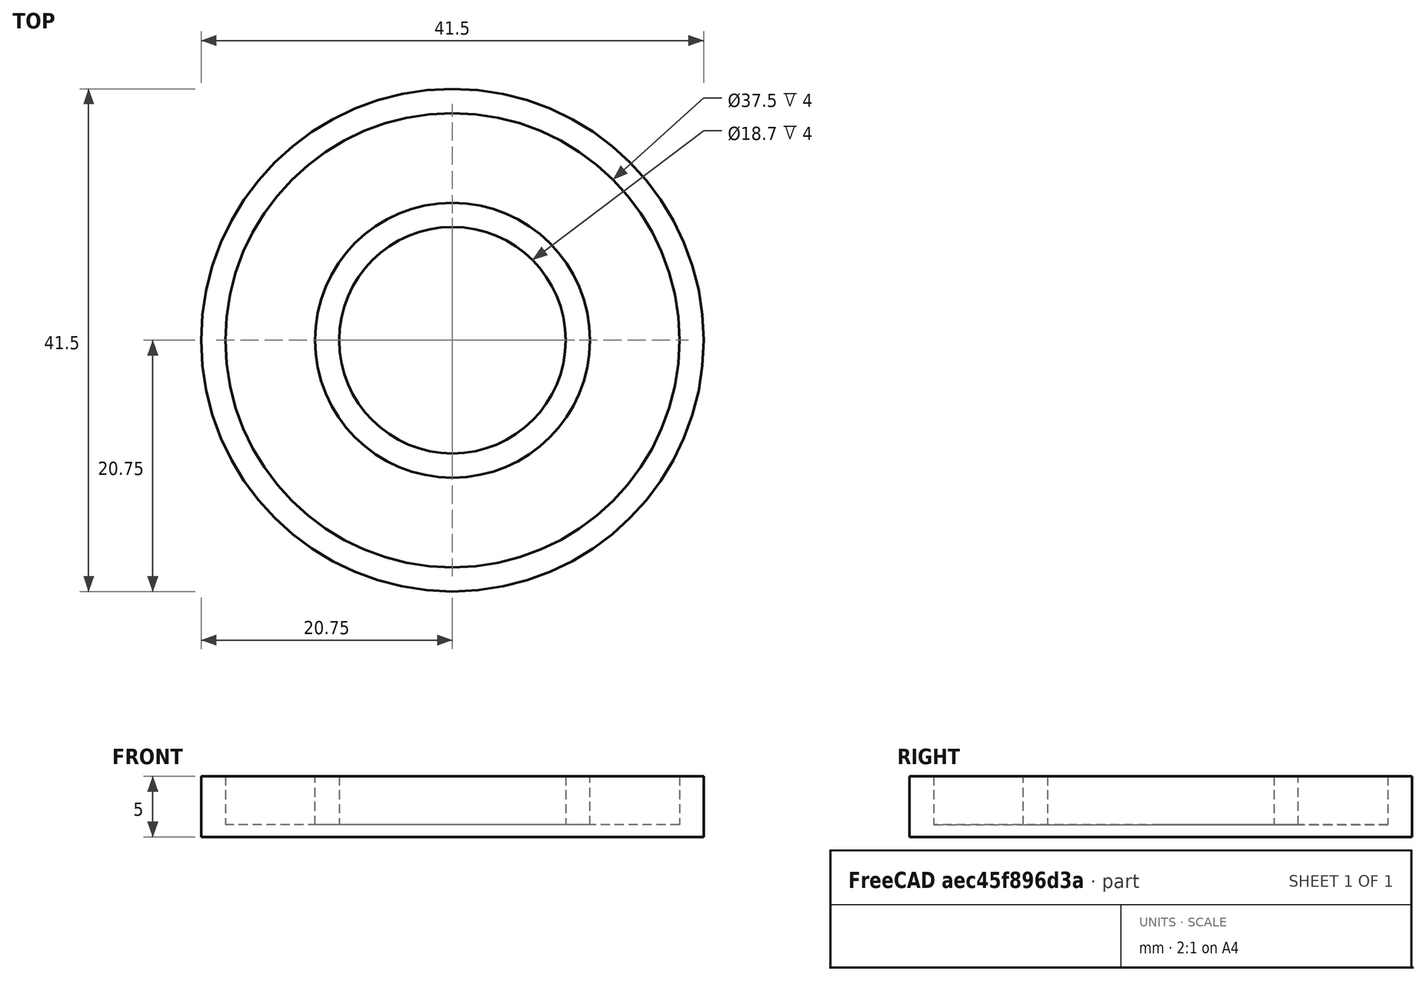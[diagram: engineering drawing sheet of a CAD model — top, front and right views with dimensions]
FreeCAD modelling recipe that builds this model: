
FCSTD DOCUMENT  (FreeCAD 0.19R24291 (Git))
Label: Крышка
License: All rights reserved
LicenseURL: http://en.wikipedia.org/wiki/All_rights_reserved
objects: Sketcher::SketchObject×1, PartDesign::Revolution×1, PartDesign::Body×1
note: 4 computed .brp shape members not serialized (recipe doc carries the construction recipe); baked Part::Feature solids carry a one-line shape summary decoded from their .brp

FEATURE [Sketcher::SketchObject] Sketch
  FullyConstrained = true
  MapMode = 5
  Placement = pos=(0,0,0) rot=(1,0,0;1.5708rad)
  Support = -> [XZ_Plane]
  sketch-geometry (10):
    g0: LineSegment StartX=0 StartY=0 StartZ=0 EndX=20.75 EndY=0 EndZ=0
    g1: LineSegment StartX=0 StartY=1 StartZ=0 EndX=0 EndY=0 EndZ=0
    g2: LineSegment StartX=11.35 StartY=1 StartZ=0 EndX=11.35 EndY=5 EndZ=0
    g3: LineSegment StartX=11.35 StartY=5 StartZ=0 EndX=9.35 EndY=5 EndZ=0
    g4: LineSegment StartX=9.35 StartY=5 StartZ=0 EndX=9.35 EndY=1 EndZ=0
    g5: LineSegment StartX=20.75 StartY=0 StartZ=0 EndX=20.75 EndY=5 EndZ=0
    g6: LineSegment StartX=20.75 StartY=5 StartZ=0 EndX=18.75 EndY=5 EndZ=0
    g7: LineSegment StartX=18.75 StartY=5 StartZ=0 EndX=18.75 EndY=1 EndZ=0
    g8: LineSegment StartX=18.75 StartY=1 StartZ=0 EndX=11.35 EndY=1 EndZ=0
    g9: LineSegment StartX=9.35 StartY=1 StartZ=0 EndX=0 EndY=1 EndZ=0
  constraints (28):
    c: Coincident(g9,g1)
    c: Coincident(g1,g0)
    c: Horizontal(g0)
    c: Vertical(g1)
    c: Coincident(g0,g-1)
    c: Coincident(g2,g3)
    c: Coincident(g3,g4)
    c: Horizontal(g3)
    c: Vertical(g2)
    c: Vertical(g4)
    c: Coincident(g5,g6)
    c: Coincident(g6,g7)
    c: Horizontal(g6)
    c: Vertical(g5)
    c: Vertical(g7)
    c: Tangent(g8,g9)
    c: Horizontal(g6,g2)
    c: Distance(g0) = 20.75
    c: Distance(g9) = 9.35
    c: Coincident(g4,g9)
    c: Distance(g3) = 2
    c: Coincident(g2,g8)
    c: Coincident(g5,g0)
    c: Coincident(g8,g7)
    c: Horizontal(g8)
    c: Equal(g6,g3)
    c: Distance(g5) = 5
    c: Distance(g1) = 1
FEATURE [PartDesign::Revolution] Revolution
  Angle = 360
  Axis = (0,2e-16,1)
  Base = (0,0,0)
  Placement = pos=(0,0,0) rot=(1,0,0;1.5708rad)
  Profile = -> Sketch
  ReferenceAxis = -> Sketch [V_Axis]
  Reversed = true
FEATURE [PartDesign::Body] Body
  Group = -> [Sketch,Revolution]
  Origin = -> Origin
  Tip = -> Revolution
